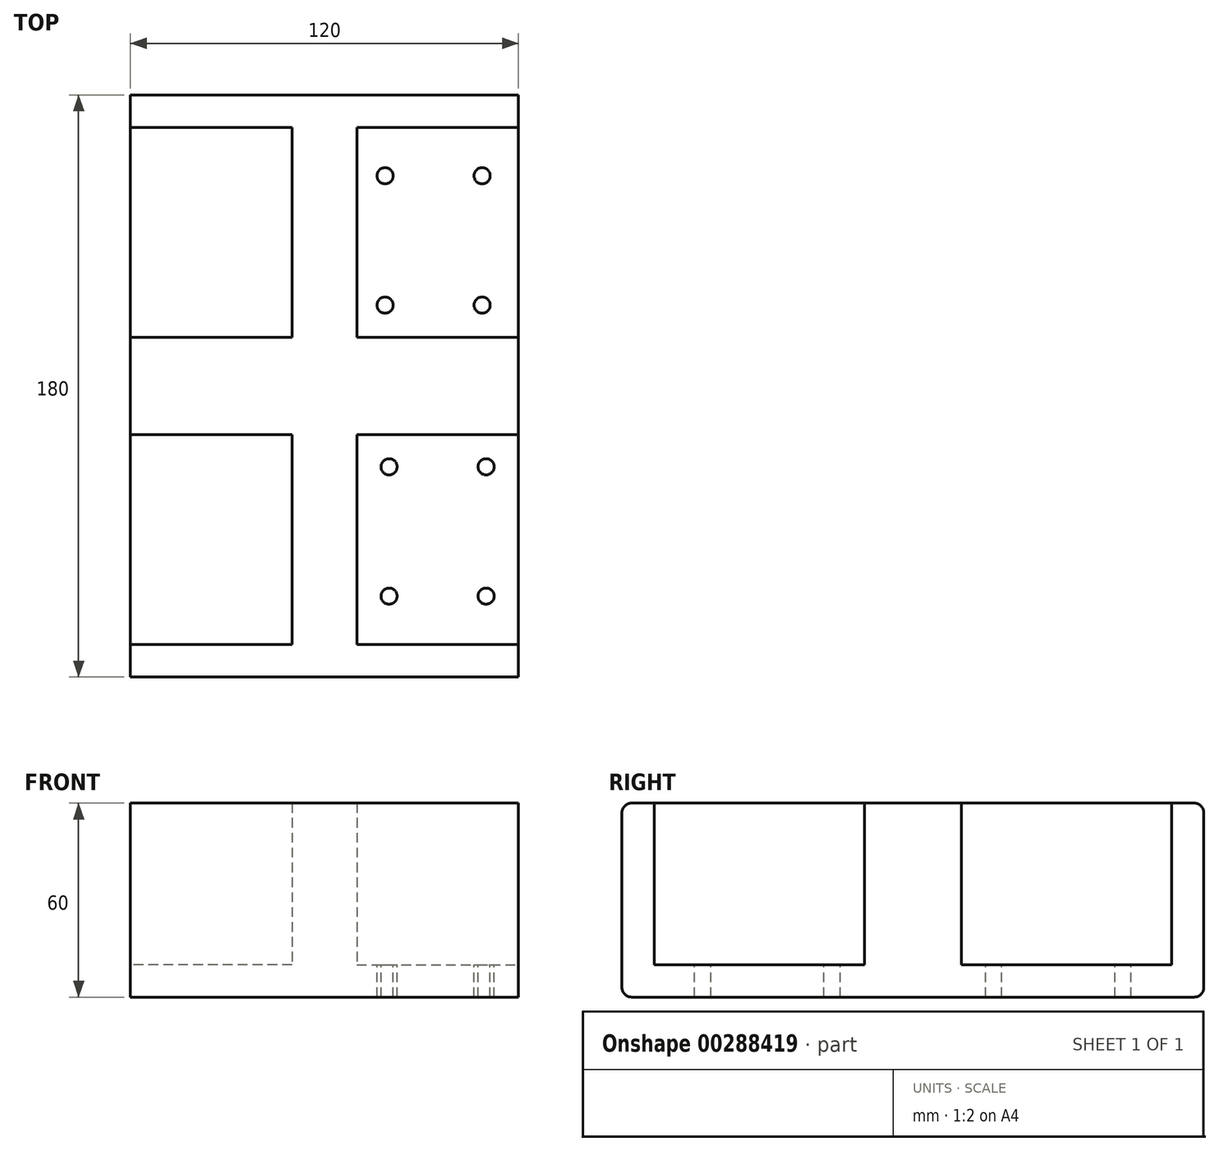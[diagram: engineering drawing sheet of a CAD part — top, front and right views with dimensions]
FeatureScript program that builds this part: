
annotation { "Feature Type Name" : "Feature", "Feature Type Description" : "" }
export const myFeature = defineFeature(function(context is Context, id is Id, definition is map)
    precondition{}
    {
        {
            var Q0;
            Q0=qCreatedBy(makeId("Top.planeOp"),FACE);
            var sketch = newSketch(context, id + "F0", { "sketchPlane" : qUnion([Q0])});
            skLineSegment(sketch, "E0.bottom", {"start": v(60, -90) * mm, "end": v(-60, -90) * mm});
            skLineSegment(sketch, "E0.top", {"start": v(60, 90) * mm, "end": v(-60, 90) * mm});
            skLineSegment(sketch, "E0.left", {"start": v(60, -90) * mm, "end": v(60, 90) * mm});
            skLineSegment(sketch, "E0.right", {"start": v(-60, -90) * mm, "end": v(-60, 90) * mm});
            skPoint(sketch, "E0.middle", {"position": v(0, 0) * mm});
            skSolve(sketch);
        }
        {
            var Q0;
            Q0=makeQuery(id+"F0.imprint","IMPRINT",FACE,{"disambiguationData":[TD([[makeQuery(id+"F0.imprint","IMPRINT",EDGE,{"derivedFrom":sQuery(id+"F0.wireOp",EDGE,"E0.bottom")}),-1.0]])]});
            extrude(context, id + "F1", {"entities" : qUnion([Q0]), "endBound" : BoundingType.SYMMETRIC, "depth" : 60 * mm});
        }
        {
            var Q0;
            Q0=makeQuery(id+"F1.opExtrude","SWEPT_FACE",FACE,{"disambiguationData":[OSD([sQuery(id+"F0.wireOp",EDGE,"E0.left")])]});
            var sketch = newSketch(context, id + "F2", { "sketchPlane" : qUnion([Q0])});
            skLineSegment(sketch, "E1.bottom", {"start": v(-80, 30) * mm, "end": v(-15, 30) * mm});
            skLineSegment(sketch, "E1.top", {"start": v(-80, -20) * mm, "end": v(-15, -20) * mm});
            skLineSegment(sketch, "E1.left", {"start": v(-80, 30) * mm, "end": v(-80, -20) * mm});
            skLineSegment(sketch, "E1.right", {"start": v(-15, 30) * mm, "end": v(-15, -20) * mm});
            skLineSegment(sketch, "E2.bottom", {"start": v(15, 30) * mm, "end": v(80, 30) * mm});
            skLineSegment(sketch, "E2.top", {"start": v(15, -20) * mm, "end": v(80, -20) * mm});
            skLineSegment(sketch, "E2.left", {"start": v(15, 30) * mm, "end": v(15, -20) * mm});
            skLineSegment(sketch, "E2.right", {"start": v(80, 30) * mm, "end": v(80, -20) * mm});
            skSolve(sketch);
        }
        {
            var Q0;
            Q0=makeQuery(id+"F1.opExtrude","SWEPT_FACE",FACE,{"disambiguationData":[OSD([sQuery(id+"F0.wireOp",EDGE,"E0.right")])]});
            var sketch = newSketch(context, id + "F3", { "sketchPlane" : qUnion([Q0])});
            skLineSegment(sketch, "E3.bottom", {"start": v(-80, 30) * mm, "end": v(-15, 30) * mm});
            skLineSegment(sketch, "E3.top", {"start": v(-80, -20) * mm, "end": v(-15, -20) * mm});
            skLineSegment(sketch, "E3.left", {"start": v(-80, 30) * mm, "end": v(-80, -20) * mm});
            skLineSegment(sketch, "E3.right", {"start": v(-15, 30) * mm, "end": v(-15, -20) * mm});
            skLineSegment(sketch, "E4.bottom", {"start": v(15, 30) * mm, "end": v(80, 30) * mm});
            skLineSegment(sketch, "E4.top", {"start": v(15, -20) * mm, "end": v(80, -20) * mm});
            skLineSegment(sketch, "E4.left", {"start": v(15, 30) * mm, "end": v(15, -20) * mm});
            skLineSegment(sketch, "E4.right", {"start": v(80, 30) * mm, "end": v(80, -20) * mm});
            skSolve(sketch);
        }
        {
            var Q0;
            Q0 = qSketchRegion(id + "F2", true);
            extrude(context, id + "F4", {"entities" : qUnion([Q0]), "operationType" : NewBodyOperationType.REMOVE, "oppositeDirection" : true, "depth" : 50 * mm, "hasDraft" : true, "draftAngle" : 0 * degree});
        }
        {
            var Q0;
            Q0=makeQuery(id+"F3.imprint","IMPRINT",FACE,{"disambiguationData":[TD([[makeQuery(id+"F3.imprint","IMPRINT",EDGE,{"derivedFrom":sQuery(id+"F3.wireOp",EDGE,"E3.bottom")}),1.0]])]});
            var Q1;
            Q1=makeQuery(id+"F3.imprint","IMPRINT",FACE,{"disambiguationData":[TD([[makeQuery(id+"F3.imprint","IMPRINT",EDGE,{"derivedFrom":sQuery(id+"F3.wireOp",EDGE,"E4.bottom")}),1.0]])]});
            extrude(context, id + "F5", {"entities" : qUnion([Q0, Q1]), "operationType" : NewBodyOperationType.REMOVE, "oppositeDirection" : true, "depth" : 50 * mm});
        }
        {
            var Q0;
            Q0=makeQuery(id+"F1.opExtrude","CAP_EDGE",EDGE,{"disambiguationData":[OSD([sQuery(id+"F0.wireOp",EDGE,"E0.bottom")])],"isStart":false});
            var Q1;
            Q1=makeQuery(id+"F1.opExtrude","CAP_EDGE",EDGE,{"disambiguationData":[OSD([sQuery(id+"F0.wireOp",EDGE,"E0.top")])],"isStart":false});
            var Q2;
            Q2=makeQuery(id+"F1.opExtrude","CAP_EDGE",EDGE,{"disambiguationData":[OSD([sQuery(id+"F0.wireOp",EDGE,"E0.bottom")])],"isStart":true});
            var Q3;
            Q3=makeQuery(id+"F1.opExtrude","CAP_EDGE",EDGE,{"disambiguationData":[OSD([sQuery(id+"F0.wireOp",EDGE,"E0.top")])],"isStart":true});
            fillet(context, id + "F6", {"entities" : qUnion([Q0, Q1, Q2, Q3]), "radius" : 3 * mm, "tangentPropagation" : true, "allowEdgeOverflow" : false});
        }
        {
            var Q0;
            Q0=makeQuery(id+"F4.boolean.opBoolean","COPY",FACE,{"derivedFrom":makeQuery(id+"F4.opExtrude","SWEPT_FACE",FACE,{"disambiguationData":[OSD([sQuery(id+"F2.wireOp",EDGE,"E1.top")])]})});
            var sketch = newSketch(context, id + "F7", { "sketchPlane" : qUnion([Q0])});
            skCircle(sketch, "E5", {"center": v(20, -65) * mm, "radius": 2.5 * mm});
            skCircle(sketch, "E6", {"center": v(20, -25) * mm, "radius": 2.5 * mm});
            skCircle(sketch, "E7", {"center": v(50, -25) * mm, "radius": 2.5 * mm});
            skCircle(sketch, "E8", {"center": v(50, -65) * mm, "radius": 2.5 * mm});
            skCircle(sketch, "E9", {"center": v(18.76, 25) * mm, "radius": 2.5 * mm});
            skCircle(sketch, "E10", {"center": v(18.76, 65) * mm, "radius": 2.5 * mm});
            skCircle(sketch, "E11", {"center": v(48.76, 65) * mm, "radius": 2.5 * mm});
            skCircle(sketch, "E12", {"center": v(48.76, 25) * mm, "radius": 2.5 * mm});
            skCircle(sketch, "E13", {"center": v(-15, -25) * mm, "radius": 2.5 * mm});
            skSolve(sketch);
        }
        {
            var Q0;
            Q0=makeQuery(id+"F7.imprint","IMPRINT",FACE,{"disambiguationData":[TD([[makeQuery(id+"F7.imprint","IMPRINT",EDGE,{"derivedFrom":sQuery(id+"F7.wireOp",EDGE,"E8")}),1.0]])]});
            var Q1;
            Q1=makeQuery(id+"F7.imprint","IMPRINT",FACE,{"disambiguationData":[TD([[makeQuery(id+"F7.imprint","IMPRINT",EDGE,{"derivedFrom":sQuery(id+"F7.wireOp",EDGE,"E7")}),1.0]])]});
            var Q2;
            Q2=makeQuery(id+"F7.imprint","IMPRINT",FACE,{"disambiguationData":[TD([[makeQuery(id+"F7.imprint","IMPRINT",EDGE,{"derivedFrom":sQuery(id+"F7.wireOp",EDGE,"E5")}),1.0]])]});
            var Q3;
            Q3=makeQuery(id+"F7.imprint","IMPRINT",FACE,{"disambiguationData":[TD([[makeQuery(id+"F7.imprint","IMPRINT",EDGE,{"derivedFrom":sQuery(id+"F7.wireOp",EDGE,"E6")}),1.0]])]});
            var Q4;
            Q4=makeQuery(id+"F7.imprint","IMPRINT",FACE,{"disambiguationData":[TD([[makeQuery(id+"F7.imprint","IMPRINT",EDGE,{"derivedFrom":sQuery(id+"F7.wireOp",EDGE,"E12")}),1.0]])]});
            var Q5;
            Q5=makeQuery(id+"F7.imprint","IMPRINT",FACE,{"disambiguationData":[TD([[makeQuery(id+"F7.imprint","IMPRINT",EDGE,{"derivedFrom":sQuery(id+"F7.wireOp",EDGE,"E9")}),1.0]])]});
            var Q6;
            Q6=makeQuery(id+"F7.imprint","IMPRINT",FACE,{"disambiguationData":[TD([[makeQuery(id+"F7.imprint","IMPRINT",EDGE,{"derivedFrom":sQuery(id+"F7.wireOp",EDGE,"E10")}),1.0]])]});
            var Q7;
            Q7=makeQuery(id+"F7.imprint","IMPRINT",FACE,{"disambiguationData":[TD([[makeQuery(id+"F7.imprint","IMPRINT",EDGE,{"derivedFrom":sQuery(id+"F7.wireOp",EDGE,"E11")}),1.0]])]});
            var Q8;
            Q8=sQuery(id+"F7.wireOp",EDGE,"E5");
            var Q9;
            Q9=sQuery(id+"F7.wireOp",EDGE,"E6");
            var Q10;
            Q10=sQuery(id+"F7.wireOp",EDGE,"E7");
            var Q11;
            Q11=sQuery(id+"F7.wireOp",EDGE,"E8");
            extrude(context, id + "F8", {"entities" : qUnion([Q0, Q1, Q2, Q3, Q4, Q5, Q6, Q7]), "operationType" : NewBodyOperationType.REMOVE, "surfaceEntities" : qUnion([Q8, Q9, Q10, Q11]), "oppositeDirection" : true, "depth" : 25 * mm, "hasSecondDirection" : true, "secondDirectionOppositeDirection" : false, "secondDirectionDepth" : 25 * mm});
        }
    });
